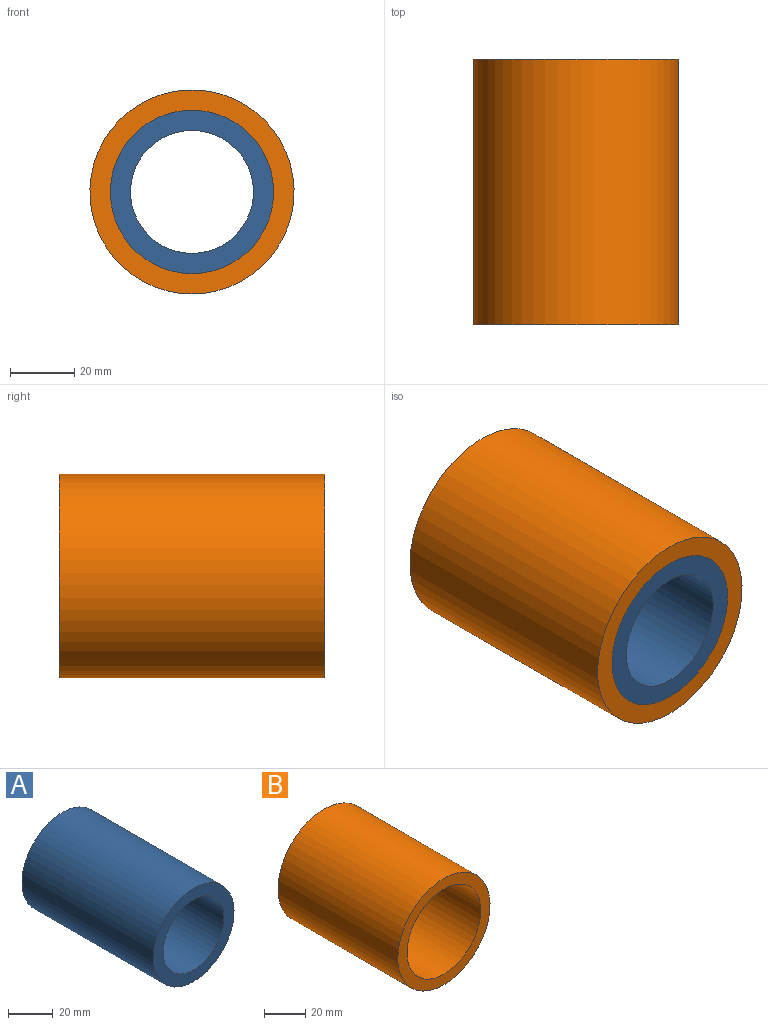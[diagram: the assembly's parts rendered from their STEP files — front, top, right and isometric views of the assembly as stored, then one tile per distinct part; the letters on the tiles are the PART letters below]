
ASSEMBLY  parts=2 mates=1
PART A: 4 faces, bbox 50.8x82.6x50.8 mm
  f0: cylinder r=19.11mm len=82.55mm, axis (0,-1,0), area 9913.7mm2, adj f2,f3
  f1: cylinder r=25.4mm len=82.55mm, axis (0,-1,0), area 13174.4mm2, adj f2,f3
  f2: plane 50.8x50.8mm, normal (0,1,0), area 879.1mm2, adj f0,f1
  f3: plane 50.8x50.8mm, normal (0,-1,0), area 879.1mm2, adj f0,f1
PART B: 4 faces, bbox 63.5x82.6x63.5 mm
  f0: cylinder r=25.4mm len=82.55mm, axis (0,-1,0), area 13174.4mm2, adj f2,f3
  f1: cylinder r=31.75mm len=82.55mm, axis (0,-1,0), area 16468mm2, adj f2,f3
  f2: plane 63.5x63.5mm, normal (0,1,0), area 1140.1mm2, adj f0,f1
  f3: plane 63.5x63.5mm, normal (0,-1,0), area 1140.1mm2, adj f0,f1
PLACE A t=(111.35,0,0)mm
PLACE B at identity
MATE cylindrical A.f0 <-> B.f0  axis (0,-1,0) through (0,41.28,102.03)mm
